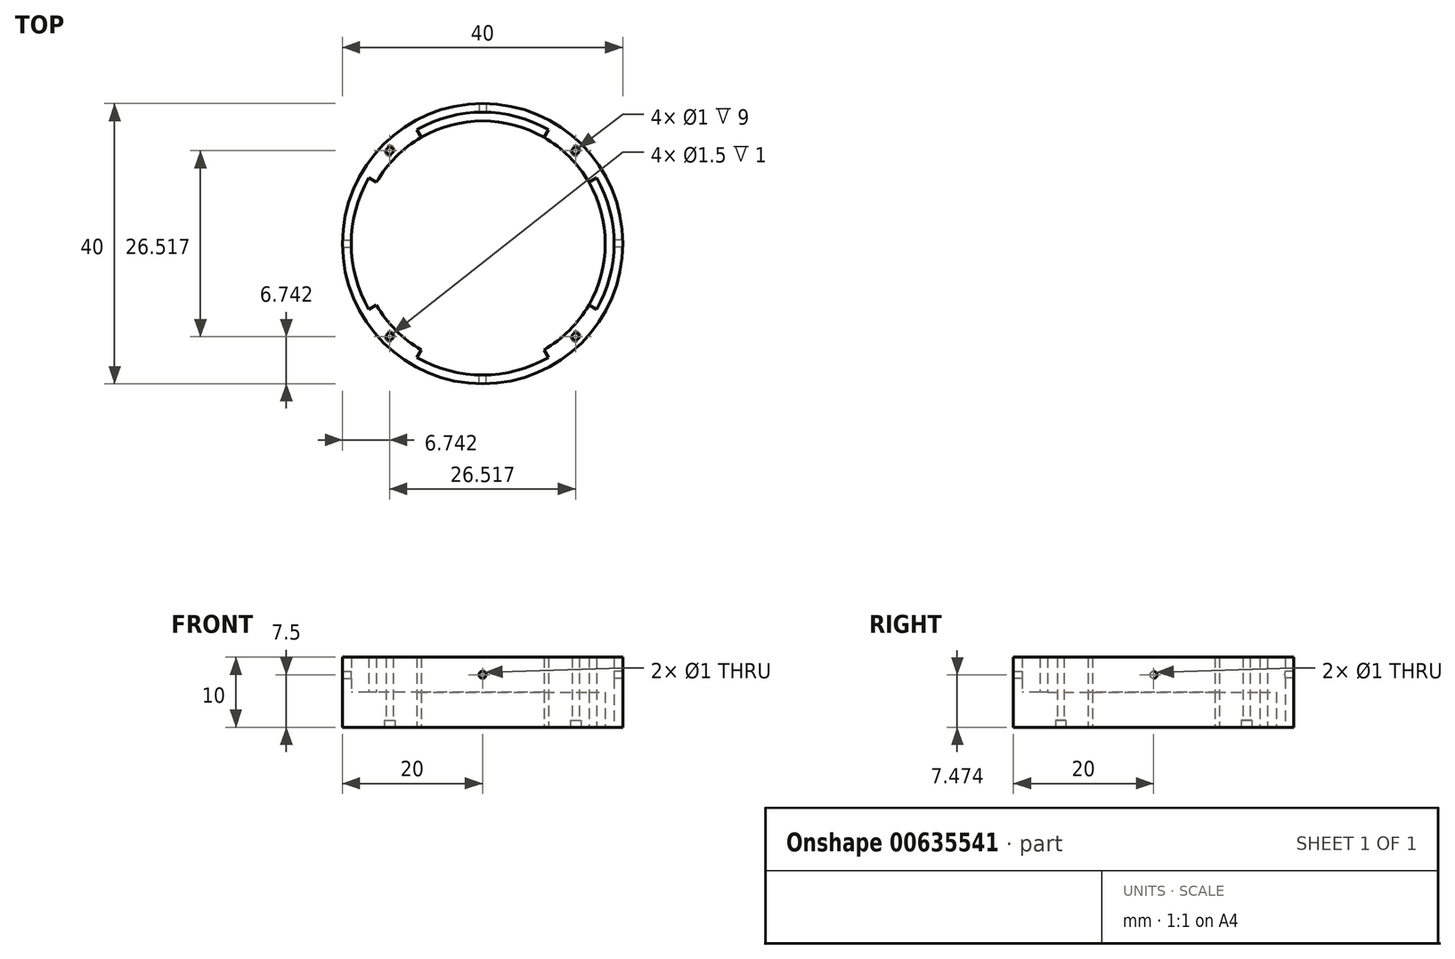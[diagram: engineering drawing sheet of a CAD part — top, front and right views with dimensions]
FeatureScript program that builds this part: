
annotation { "Feature Type Name" : "Feature", "Feature Type Description" : "" }
export const myFeature = defineFeature(function(context is Context, id is Id, definition is map)
    precondition{}
    {
        {
            var Q0;
            Q0=qCreatedBy(makeId("Top.planeOp"),FACE);
            var sketch = newSketch(context, id + "F0", { "sketchPlane" : qUnion([Q0])});
            skCircle(sketch, "E0", {"center": v(0, 0) * mm, "radius": 17.5 * mm, "construction": true});
            skCircle(sketch, "E1", {"center": v(0, 0) * mm, "radius": 18.75 * mm, "construction": true});
            skLineSegment(sketch, "E2", {"start": v(0, 0) * mm, "end": v(-16.24, 9.38) * mm, "construction": true});
            skLineSegment(sketch, "E3.MirrorCS", {"start": v(0, 0) * mm, "end": v(-16.24, -9.38) * mm, "construction": true});
            skLineSegment(sketch, "E4", {"start": v(0, 0) * mm, "end": v(-9.37, 16.24) * mm, "construction": true});
            skLineSegment(sketch, "E5.MirrorCS", {"start": v(0, 0) * mm, "end": v(9.37, 16.24) * mm, "construction": true});
            skLineSegment(sketch, "E6", {"start": v(0, 0) * mm, "end": v(16.24, 9.38) * mm, "construction": true});
            skLineSegment(sketch, "E7.MirrorCS", {"start": v(0, 0) * mm, "end": v(16.24, -9.38) * mm, "construction": true});
            skLineSegment(sketch, "E8", {"start": v(0, 0) * mm, "end": v(9.38, -16.24) * mm, "construction": true});
            skLineSegment(sketch, "E9.MirrorCS", {"start": v(0, 0) * mm, "end": v(-9.38, -16.24) * mm, "construction": true});
            skArc(sketch, "E10", {"start": v(-15.16, 8.75) * mm, "mid": v(-17.5, 0) * mm, "end": v(-15.16, -8.75) * mm});
            skArc(sketch, "E11", {"start": v(-16.24, 9.38) * mm, "mid": v(-18.75, 0) * mm, "end": v(-16.24, -9.38) * mm});
            skArc(sketch, "E12", {"start": v(-8.75, -15.16) * mm, "mid": v(0, -17.5) * mm, "end": v(8.75, -15.16) * mm});
            skArc(sketch, "E13", {"start": v(-9.38, -16.24) * mm, "mid": v(0, -18.75) * mm, "end": v(9.38, -16.24) * mm});
            skArc(sketch, "E14", {"start": v(-8.75, 15.16) * mm, "mid": v(0, 17.5) * mm, "end": v(8.75, 15.16) * mm});
            skArc(sketch, "E15", {"start": v(-9.37, 16.24) * mm, "mid": v(0, 18.75) * mm, "end": v(9.37, 16.24) * mm});
            skArc(sketch, "E16", {"start": v(15.16, 8.75) * mm, "mid": v(17.5, 0) * mm, "end": v(15.16, -8.75) * mm});
            skArc(sketch, "E17", {"start": v(16.24, 9.37) * mm, "mid": v(18.75, 0) * mm, "end": v(16.24, -9.37) * mm});
            skLineSegment(sketch, "E18", {"start": v(-8.75, 15.16) * mm, "end": v(-9.37, 16.24) * mm});
            skLineSegment(sketch, "E19", {"start": v(-15.16, 8.75) * mm, "end": v(-16.24, 9.38) * mm});
            skLineSegment(sketch, "E20", {"start": v(-15.16, -8.75) * mm, "end": v(-16.24, -9.38) * mm});
            skLineSegment(sketch, "E21", {"start": v(-8.75, -15.16) * mm, "end": v(-9.38, -16.24) * mm});
            skLineSegment(sketch, "E22", {"start": v(8.75, -15.16) * mm, "end": v(9.38, -16.24) * mm});
            skLineSegment(sketch, "E23", {"start": v(15.16, -8.75) * mm, "end": v(16.24, -9.38) * mm});
            skLineSegment(sketch, "E24", {"start": v(15.16, 8.75) * mm, "end": v(16.24, 9.38) * mm});
            skLineSegment(sketch, "E25", {"start": v(8.75, 15.16) * mm, "end": v(9.38, 16.24) * mm});
            skArc(sketch, "E26", {"start": v(-15.16, 8.75) * mm, "mid": v(-12.37, 12.37) * mm, "end": v(-8.75, 15.16) * mm});
            skArc(sketch, "E27", {"start": v(-16.24, 9.38) * mm, "mid": v(-13.26, 13.26) * mm, "end": v(-9.37, 16.24) * mm});
            skArc(sketch, "E28", {"start": v(8.75, 15.16) * mm, "mid": v(12.37, 12.37) * mm, "end": v(15.16, 8.75) * mm});
            skArc(sketch, "E29", {"start": v(9.37, 16.24) * mm, "mid": v(13.26, 13.26) * mm, "end": v(16.24, 9.37) * mm});
            skArc(sketch, "E30", {"start": v(15.16, -8.75) * mm, "mid": v(12.37, -12.37) * mm, "end": v(8.75, -15.16) * mm});
            skArc(sketch, "E31", {"start": v(16.24, -9.38) * mm, "mid": v(13.26, -13.26) * mm, "end": v(9.38, -16.24) * mm});
            skArc(sketch, "E32", {"start": v(-8.75, -15.16) * mm, "mid": v(-12.37, -12.37) * mm, "end": v(-15.16, -8.75) * mm});
            skArc(sketch, "E33", {"start": v(-9.38, -16.24) * mm, "mid": v(-13.26, -13.26) * mm, "end": v(-16.24, -9.38) * mm});
            skCircle(sketch, "E34", {"center": v(0, 0) * mm, "radius": 20 * mm});
            skLineSegment(sketch, "E35", {"start": v(0, 0) * mm, "end": v(-13.26, -13.26) * mm, "construction": true});
            skLineSegment(sketch, "E36", {"start": v(0, 0) * mm, "end": v(13.26, -13.26) * mm, "construction": true});
            skLineSegment(sketch, "E37.MirrorCS", {"start": v(0, 0) * mm, "end": v(13.26, 13.26) * mm, "construction": true});
            skLineSegment(sketch, "E38.MirrorCS", {"start": v(0, 0) * mm, "end": v(-13.26, 13.26) * mm, "construction": true});
            skSolve(sketch);
        }
        {
            var Q0;
            Q0=makeQuery(id+"F0.imprint","IMPRINT",FACE,{"disambiguationData":[TD([[makeQuery(id+"F0.imprint","IMPRINT",EDGE,{"derivedFrom":sQuery(id+"F0.wireOp",EDGE,"E11")}),-1.0]])]});
            extrude(context, id + "F1", {"entities" : qUnion([Q0]), "depth" : 10 * mm, "offsetDistance" : 25 * mm});
        }
        {
            var Q0;
            Q0=makeQuery(id+"F0.imprint","IMPRINT",FACE,{"disambiguationData":[TD([[makeQuery(id+"F0.imprint","IMPRINT",EDGE,{"derivedFrom":sQuery(id+"F0.wireOp",EDGE,"E10")}),-1.0]])]});
            extrude(context, id + "F2", {"entities" : qUnion([Q0]), "operationType" : NewBodyOperationType.ADD, "depth" : 5 * mm, "offsetDistance" : 25 * mm});
        }
        {
            var Q0;
            Q0=makeQuery(id+"F0.imprint","IMPRINT",FACE,{"disambiguationData":[TD([[makeQuery(id+"F0.imprint","IMPRINT",EDGE,{"derivedFrom":sQuery(id+"F0.wireOp",EDGE,"E14")}),1.0]])]});
            extrude(context, id + "F3", {"entities" : qUnion([Q0]), "operationType" : NewBodyOperationType.ADD, "depth" : 5 * mm, "offsetDistance" : 25 * mm});
        }
        {
            var Q0;
            Q0=makeQuery(id+"F0.imprint","IMPRINT",FACE,{"disambiguationData":[TD([[makeQuery(id+"F0.imprint","IMPRINT",EDGE,{"derivedFrom":sQuery(id+"F0.wireOp",EDGE,"E12")}),-1.0]])]});
            extrude(context, id + "F4", {"entities" : qUnion([Q0]), "operationType" : NewBodyOperationType.ADD, "depth" : 5 * mm, "offsetDistance" : 25 * mm});
        }
        {
            var Q0;
            Q0=makeQuery(id+"F0.imprint","IMPRINT",FACE,{"disambiguationData":[TD([[makeQuery(id+"F0.imprint","IMPRINT",EDGE,{"derivedFrom":sQuery(id+"F0.wireOp",EDGE,"E16")}),1.0]])]});
            extrude(context, id + "F5", {"entities" : qUnion([Q0]), "operationType" : NewBodyOperationType.ADD, "depth" : 5 * mm, "offsetDistance" : 25 * mm});
        }
        {
            var Q0;
            Q0=makeQuery(id+"F0.imprint","IMPRINT",FACE,{"disambiguationData":[TD([[makeQuery(id+"F0.imprint","IMPRINT",EDGE,{"derivedFrom":sQuery(id+"F0.wireOp",EDGE,"E18")}),1.0]])]});
            extrude(context, id + "F6", {"entities" : qUnion([Q0]), "operationType" : NewBodyOperationType.ADD, "depth" : 10 * mm, "offsetDistance" : 25 * mm});
        }
        {
            var Q0;
            Q0=makeQuery(id+"F0.imprint","IMPRINT",FACE,{"disambiguationData":[TD([[makeQuery(id+"F0.imprint","IMPRINT",EDGE,{"derivedFrom":sQuery(id+"F0.wireOp",EDGE,"E20")}),1.0]])]});
            extrude(context, id + "F7", {"entities" : qUnion([Q0]), "operationType" : NewBodyOperationType.ADD, "depth" : 10 * mm, "offsetDistance" : 25 * mm});
        }
        {
            var Q0;
            Q0=makeQuery(id+"F0.imprint","IMPRINT",FACE,{"disambiguationData":[TD([[makeQuery(id+"F0.imprint","IMPRINT",EDGE,{"derivedFrom":sQuery(id+"F0.wireOp",EDGE,"E22")}),1.0]])]});
            extrude(context, id + "F8", {"entities" : qUnion([Q0]), "operationType" : NewBodyOperationType.ADD, "depth" : 10 * mm, "offsetDistance" : 25 * mm});
        }
        {
            var Q0;
            Q0=makeQuery(id+"F0.imprint","IMPRINT",FACE,{"disambiguationData":[TD([[makeQuery(id+"F0.imprint","IMPRINT",EDGE,{"derivedFrom":sQuery(id+"F0.wireOp",EDGE,"E24")}),1.0]])]});
            extrude(context, id + "F9", {"entities" : qUnion([Q0]), "operationType" : NewBodyOperationType.ADD, "depth" : 10 * mm, "offsetDistance" : 25 * mm});
        }
        {
            var Q0;
            Q0=qCreatedBy(makeId("Front.planeOp"),FACE);
            var sketch = newSketch(context, id + "F10", { "sketchPlane" : qUnion([Q0])});
            skLineSegment(sketch, "E39", {"start": v(25, 7.5) * mm, "end": v(-25, 7.5) * mm, "construction": true});
            skCircle(sketch, "E40", {"center": v(0, 7.5) * mm, "radius": 1 * mm, "construction": true});
            skLineSegment(sketch, "E41", {"start": v(0, 7.5) * mm, "end": v(0, 0) * mm, "construction": true});
            skLineSegment(sketch, "E42", {"start": v(-25, 0) * mm, "end": v(25, 0) * mm, "construction": true});
            skLineSegment(sketch, "E43", {"start": v(-21.25, 0) * mm, "end": v(-21.25, 7.5) * mm});
            skSolve(sketch);
        }
        {
            var Q0;
            Q0=qCreatedBy(makeId("Right.planeOp"),FACE);
            var sketch = newSketch(context, id + "F11", { "sketchPlane" : qUnion([Q0])});
            skLineSegment(sketch, "E44", {"start": v(0, 7.47) * mm, "end": v(21.25, 7.47) * mm, "construction": true});
            skSolve(sketch);
        }
        {
            var Q0;
            Q0=sQuery(id+"F11.wireOp",VERTEX,"E44.start");
            var Q1;
            Q1=makeQuery(id+"F1.opExtrude","SWEPT_BODY",BODY,{"disambiguationData":[OSD([sQuery(id+"F0.wireOp",EDGE,"E11"),sQuery(id+"F0.wireOp",EDGE,"E13"),sQuery(id+"F0.wireOp",EDGE,"E15"),sQuery(id+"F0.wireOp",EDGE,"E17"),sQuery(id+"F0.wireOp",EDGE,"E27"),sQuery(id+"F0.wireOp",EDGE,"E29"),sQuery(id+"F0.wireOp",EDGE,"E31"),sQuery(id+"F0.wireOp",EDGE,"E33"),sQuery(id+"F0.wireOp",EDGE,"E34")])]});
            hole(context, id + "F12", {"style" : HoleStyle.SIMPLE, "endStyle" : HoleEndStyle.THROUGH, "holeDiameter" : 1 * mm, "majorDiameter" : 5 * mm, "isTappedThrough" : true, "tappedDepth" : 12 * mm, "tapClearance" : 3, "locations" : qUnion([Q0]), "scope" : qUnion([Q1])});
        }
        {
            var Q0;
            Q0=sQuery(id+"F10.wireOp",VERTEX,"E40.center");
            var Q1;
            Q1=makeQuery(id+"F1.opExtrude","SWEPT_BODY",BODY,{"disambiguationData":[OSD([sQuery(id+"F0.wireOp",EDGE,"E11"),sQuery(id+"F0.wireOp",EDGE,"E13"),sQuery(id+"F0.wireOp",EDGE,"E15"),sQuery(id+"F0.wireOp",EDGE,"E17"),sQuery(id+"F0.wireOp",EDGE,"E27"),sQuery(id+"F0.wireOp",EDGE,"E29"),sQuery(id+"F0.wireOp",EDGE,"E31"),sQuery(id+"F0.wireOp",EDGE,"E33"),sQuery(id+"F0.wireOp",EDGE,"E34")])]});
            hole(context, id + "F13", {"style" : HoleStyle.SIMPLE, "endStyle" : HoleEndStyle.THROUGH, "holeDiameter" : 1 * mm, "majorDiameter" : 5 * mm, "isTappedThrough" : true, "tappedDepth" : 12 * mm, "tapClearance" : 3, "locations" : qUnion([Q0]), "scope" : qUnion([Q1])});
        }
        {
            var Q0;
            Q0=sQuery(id+"F10.wireOp",VERTEX,"E40.center");
            var Q1;
            Q1=makeQuery(id+"F1.opExtrude","SWEPT_BODY",BODY,{"disambiguationData":[OSD([sQuery(id+"F0.wireOp",EDGE,"E11"),sQuery(id+"F0.wireOp",EDGE,"E13"),sQuery(id+"F0.wireOp",EDGE,"E15"),sQuery(id+"F0.wireOp",EDGE,"E17"),sQuery(id+"F0.wireOp",EDGE,"E27"),sQuery(id+"F0.wireOp",EDGE,"E29"),sQuery(id+"F0.wireOp",EDGE,"E31"),sQuery(id+"F0.wireOp",EDGE,"E33"),sQuery(id+"F0.wireOp",EDGE,"E34")])]});
            hole(context, id + "F14", {"style" : HoleStyle.SIMPLE, "endStyle" : HoleEndStyle.THROUGH, "oppositeDirection" : true, "holeDiameter" : 1 * mm, "majorDiameter" : 5 * mm, "isTappedThrough" : true, "tappedDepth" : 12 * mm, "tapClearance" : 3, "locations" : qUnion([Q0]), "scope" : qUnion([Q1])});
        }
        {
            var Q0;
            Q0=sQuery(id+"F11.wireOp",VERTEX,"E44.start");
            var Q1;
            Q1=makeQuery(id+"F1.opExtrude","SWEPT_BODY",BODY,{"disambiguationData":[OSD([sQuery(id+"F0.wireOp",EDGE,"E11"),sQuery(id+"F0.wireOp",EDGE,"E13"),sQuery(id+"F0.wireOp",EDGE,"E15"),sQuery(id+"F0.wireOp",EDGE,"E17"),sQuery(id+"F0.wireOp",EDGE,"E27"),sQuery(id+"F0.wireOp",EDGE,"E29"),sQuery(id+"F0.wireOp",EDGE,"E31"),sQuery(id+"F0.wireOp",EDGE,"E33"),sQuery(id+"F0.wireOp",EDGE,"E34")])]});
            hole(context, id + "F15", {"style" : HoleStyle.SIMPLE, "endStyle" : HoleEndStyle.THROUGH, "oppositeDirection" : true, "holeDiameter" : 1 * mm, "majorDiameter" : 5 * mm, "isTappedThrough" : true, "tappedDepth" : 12 * mm, "tapClearance" : 3, "locations" : qUnion([Q0]), "scope" : qUnion([Q1])});
        }
        {
            var Q0;
            Q0=sQuery(id+"F0.wireOp",VERTEX,"E35.end");
            var Q1;
            Q1=makeQuery(id+"F1.opExtrude","SWEPT_BODY",BODY,{"disambiguationData":[OSD([sQuery(id+"F0.wireOp",EDGE,"E11"),sQuery(id+"F0.wireOp",EDGE,"E13"),sQuery(id+"F0.wireOp",EDGE,"E15"),sQuery(id+"F0.wireOp",EDGE,"E17"),sQuery(id+"F0.wireOp",EDGE,"E27"),sQuery(id+"F0.wireOp",EDGE,"E29"),sQuery(id+"F0.wireOp",EDGE,"E31"),sQuery(id+"F0.wireOp",EDGE,"E33"),sQuery(id+"F0.wireOp",EDGE,"E34")])]});
            hole(context, id + "F16", {"style" : HoleStyle.C_BORE, "endStyle" : HoleEndStyle.THROUGH, "oppositeDirection" : true, "holeDiameter" : 1 * mm, "cBoreDiameter" : 1.5 * mm, "cBoreDepth" : 1 * mm, "majorDiameter" : 5 * mm, "isTappedThrough" : true, "tappedDepth" : 12 * mm, "tapClearance" : 3, "locations" : qUnion([Q0]), "scope" : qUnion([Q1])});
        }
        {
            var Q0;
            Q0=sQuery(id+"F0.wireOp",VERTEX,"E36.end");
            var Q1;
            Q1=makeQuery(id+"F1.opExtrude","SWEPT_BODY",BODY,{"disambiguationData":[OSD([sQuery(id+"F0.wireOp",EDGE,"E11"),sQuery(id+"F0.wireOp",EDGE,"E13"),sQuery(id+"F0.wireOp",EDGE,"E15"),sQuery(id+"F0.wireOp",EDGE,"E17"),sQuery(id+"F0.wireOp",EDGE,"E27"),sQuery(id+"F0.wireOp",EDGE,"E29"),sQuery(id+"F0.wireOp",EDGE,"E31"),sQuery(id+"F0.wireOp",EDGE,"E33"),sQuery(id+"F0.wireOp",EDGE,"E34")])]});
            hole(context, id + "F17", {"style" : HoleStyle.C_BORE, "endStyle" : HoleEndStyle.THROUGH, "oppositeDirection" : true, "holeDiameter" : 1 * mm, "cBoreDiameter" : 1.5 * mm, "cBoreDepth" : 1 * mm, "majorDiameter" : 5 * mm, "isTappedThrough" : true, "tappedDepth" : 12 * mm, "tapClearance" : 3, "locations" : qUnion([Q0]), "scope" : qUnion([Q1])});
        }
        {
            var Q0;
            Q0=sQuery(id+"F0.wireOp",VERTEX,"E37.MirrorCS.end");
            var Q1;
            Q1=makeQuery(id+"F1.opExtrude","SWEPT_BODY",BODY,{"disambiguationData":[OSD([sQuery(id+"F0.wireOp",EDGE,"E11"),sQuery(id+"F0.wireOp",EDGE,"E13"),sQuery(id+"F0.wireOp",EDGE,"E15"),sQuery(id+"F0.wireOp",EDGE,"E17"),sQuery(id+"F0.wireOp",EDGE,"E27"),sQuery(id+"F0.wireOp",EDGE,"E29"),sQuery(id+"F0.wireOp",EDGE,"E31"),sQuery(id+"F0.wireOp",EDGE,"E33"),sQuery(id+"F0.wireOp",EDGE,"E34")])]});
            hole(context, id + "F18", {"style" : HoleStyle.C_BORE, "endStyle" : HoleEndStyle.THROUGH, "oppositeDirection" : true, "holeDiameter" : 1 * mm, "cBoreDiameter" : 1.5 * mm, "cBoreDepth" : 1 * mm, "majorDiameter" : 5 * mm, "isTappedThrough" : true, "tappedDepth" : 12 * mm, "tapClearance" : 3, "locations" : qUnion([Q0]), "scope" : qUnion([Q1])});
        }
        {
            var Q0;
            Q0=sQuery(id+"F0.wireOp",VERTEX,"E38.MirrorCS.end");
            var Q1;
            Q1=makeQuery(id+"F1.opExtrude","SWEPT_BODY",BODY,{"disambiguationData":[OSD([sQuery(id+"F0.wireOp",EDGE,"E11"),sQuery(id+"F0.wireOp",EDGE,"E13"),sQuery(id+"F0.wireOp",EDGE,"E15"),sQuery(id+"F0.wireOp",EDGE,"E17"),sQuery(id+"F0.wireOp",EDGE,"E27"),sQuery(id+"F0.wireOp",EDGE,"E29"),sQuery(id+"F0.wireOp",EDGE,"E31"),sQuery(id+"F0.wireOp",EDGE,"E33"),sQuery(id+"F0.wireOp",EDGE,"E34")])]});
            hole(context, id + "F19", {"style" : HoleStyle.C_BORE, "endStyle" : HoleEndStyle.THROUGH, "oppositeDirection" : true, "holeDiameter" : 1 * mm, "cBoreDiameter" : 1.5 * mm, "cBoreDepth" : 1 * mm, "majorDiameter" : 5 * mm, "isTappedThrough" : true, "tappedDepth" : 12 * mm, "tapClearance" : 3, "locations" : qUnion([Q0]), "scope" : qUnion([Q1])});
        }
    });
